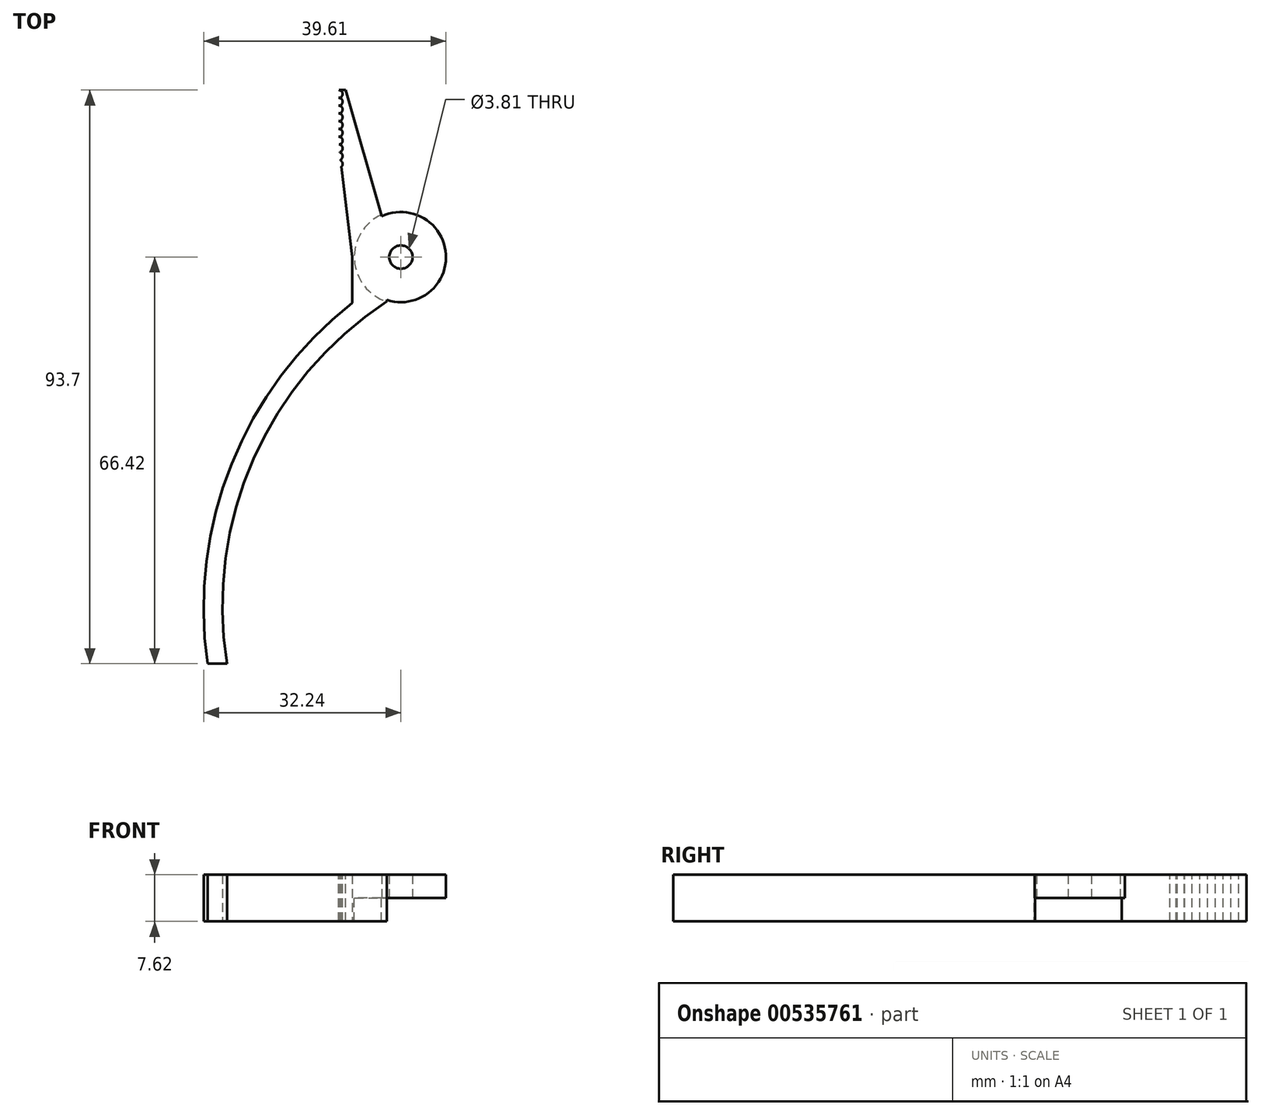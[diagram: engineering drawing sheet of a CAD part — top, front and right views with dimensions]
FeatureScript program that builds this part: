
annotation { "Feature Type Name" : "Feature", "Feature Type Description" : "" }
export const myFeature = defineFeature(function(context is Context, id is Id, definition is map)
    precondition{}
    {
        {
            var Q0;
            Q0=qCreatedBy(makeId("Top.planeOp"),FACE);
            var sketch = newSketch(context, id + "F0", { "sketchPlane" : qUnion([Q0])});
            skCircle(sketch, "E0", {"center": v(0, 0) * mm, "radius": 7.62 * mm});
            skCircle(sketch, "E1", {"center": v(0, 0) * mm, "radius": 7.37 * mm});
            skLineSegment(sketch, "E2", {"start": v(-10.16, 31.32) * mm, "end": v(-10.16, 18.62) * mm});
            skLineSegment(sketch, "E3", {"start": v(-10.16, 31.32) * mm, "end": v(-3.21, 6.91) * mm});
            skLineSegment(sketch, "E4", {"start": v(-10.16, 18.62) * mm, "end": v(-7.94, 0) * mm});
            skLineSegment(sketch, "E5", {"start": v(-7.94, 0) * mm, "end": v(-7.94, -7.49) * mm});
            skLineSegment(sketch, "E6", {"start": v(-7.94, -7.49) * mm, "end": v(-2.3, -7.26) * mm});
            skArc(sketch, "E7", {"start": v(-7.94, -7.49) * mm, "mid": v(-27.67, -33.78) * mm, "end": v(-31.6, -66.42) * mm});
            skLineSegment(sketch, "E8", {"start": v(-31.6, -66.42) * mm, "end": v(-28.43, -66.42) * mm});
            skArc(sketch, "E9", {"start": v(-2.3, -7.26) * mm, "mid": v(-24.1, -32.99) * mm, "end": v(-28.43, -66.42) * mm});
            skCircle(sketch, "E10", {"center": v(0, 0) * mm, "radius": 1.9 * mm});
            skLineSegment(sketch, "E11", {"start": v(-2.3, -7.26) * mm, "end": v(-2.3, -7) * mm});
            skLineSegment(sketch, "E12", {"start": v(-3.21, 6.91) * mm, "end": v(-3.14, 6.66) * mm});
            skSolve(sketch);
        }
        {
            var Q0;
            Q0=makeQuery(id+"F0.imprint","IMPRINT",FACE,{"disambiguationData":[TD([[makeQuery(id+"F0.imprint","IMPRINT",EDGE,{"derivedFrom":sQuery(id+"F0.wireOp",EDGE,"E6")}),-1.0]])]});
            var Q1;
            {var subQ0=sQuery(id+"F0.wireOp",EDGE,"E5");Q1=makeQuery(id+"F0.imprint","IMPRINT",FACE,{"disambiguationData":[TD([[makeQuery(id+"F0.imprint","IMPRINT",EDGE,{"derivedFrom":subQ0}),1.0]])]});}
            var Q2;
            Q2=makeQuery(id+"F0.imprint","IMPRINT",FACE,{"disambiguationData":[TD([[makeQuery(id+"F0.imprint","IMPRINT",EDGE,{"derivedFrom":sQuery(id+"F0.wireOp",EDGE,"E2")}),1.0]])]});
            var Q3;
            {var subQ0=sQuery(id+"F0.wireOp",EDGE,"E7");Q3=makeQuery(id+"F0.imprint","IMPRINT",FACE,{"disambiguationData":[TD([[makeQuery(id+"F0.imprint","IMPRINT",EDGE,{"derivedFrom":subQ0}),1.0]])]});}
            var Q4;
            Q4=makeQuery(id+"F0.imprint","IMPRINT",FACE,{"disambiguationData":[TD([[makeQuery(id+"F0.imprint","IMPRINT",EDGE,{"derivedFrom":sQuery(id+"F0.wireOp",EDGE,"E10")}),-1.0]])]});
            var Q5;
            {var subQ0=sQuery(id+"F0.wireOp",EDGE,"E11");Q5=makeQuery(id+"F0.imprint","IMPRINT",FACE,{"disambiguationData":[TD([[makeQuery(id+"F0.imprint","IMPRINT",EDGE,{"derivedFrom":subQ0}),1.0]])]});}
            extrude(context, id + "F1", {"entities" : qUnion([Q0, Q1, Q2, Q3, Q4, Q5]), "depth" : 3.8 * mm, "offsetDistance" : 25.4 * mm});
        }
        {
            var Q0;
            Q0=makeQuery(id+"F0.imprint","IMPRINT",FACE,{"disambiguationData":[TD([[makeQuery(id+"F0.imprint","IMPRINT",EDGE,{"derivedFrom":sQuery(id+"F0.wireOp",EDGE,"E2")}),1.0]])]});
            var Q1;
            {var subQ0=sQuery(id+"F0.wireOp",EDGE,"E7");Q1=makeQuery(id+"F0.imprint","IMPRINT",FACE,{"disambiguationData":[TD([[makeQuery(id+"F0.imprint","IMPRINT",EDGE,{"derivedFrom":subQ0}),1.0]])]});}
            extrude(context, id + "F2", {"entities" : qUnion([Q0, Q1]), "operationType" : NewBodyOperationType.ADD, "oppositeDirection" : true, "depth" : 3.8 * mm, "offsetDistance" : 25.4 * mm});
        }
        {
            var Q0;
            Q0=makeQuery(id+"F1.opExtrude","CAP_FACE",FACE,{"disambiguationData":[OSD([sQuery(id+"F0.wireOp",EDGE,"E1"),sQuery(id+"F0.wireOp",EDGE,"E2"),sQuery(id+"F0.wireOp",EDGE,"E3"),sQuery(id+"F0.wireOp",EDGE,"E4"),sQuery(id+"F0.wireOp",EDGE,"E5"),sQuery(id+"F0.wireOp",EDGE,"E7"),sQuery(id+"F0.wireOp",EDGE,"E8"),sQuery(id+"F0.wireOp",EDGE,"E9"),sQuery(id+"F0.wireOp",EDGE,"E10"),sQuery(id+"F0.wireOp",EDGE,"E11"),sQuery(id+"F0.wireOp",EDGE,"E12")])],"isStart":false});
            var sketch = newSketch(context, id + "F3", { "sketchPlane" : qUnion([Q0])});
            skCircle(sketch, "E13", {"center": v(-10.16, 15.22) * mm, "radius": 0.64 * mm});
            skLineSegment(sketch, "E14.direction1", {"start": v(-10.16, 15.22) * mm, "end": v(15.24, 15.22) * mm, "construction": true});
            skLineSegment(sketch, "E14.direction2", {"start": v(-10.16, 15.22) * mm, "end": v(-10.16, 16.5) * mm, "construction": true});
            skPoint(sketch, "E15.0", {"position": v(-10.16, 31.32) * mm});
            skLineSegment(sketch, "E16", {"start": v(-10.16, 27.28) * mm, "end": v(-10.16, 31.32) * mm});
            skLineSegment(sketch, "E17", {"start": v(-10.16, 27.28) * mm, "end": v(-9.01, 27.28) * mm});
            skLineSegment(sketch, "E18", {"start": v(-9.01, 27.28) * mm, "end": v(-10.16, 31.32) * mm});
            skCircle(sketch, "E19.0.0.1", {"center": v(-10.16, 16.5) * mm, "radius": 0.64 * mm});
            skCircle(sketch, "E19.0.0.2", {"center": v(-10.16, 17.76) * mm, "radius": 0.64 * mm});
            skCircle(sketch, "E19.0.0.3", {"center": v(-10.16, 19.03) * mm, "radius": 0.64 * mm});
            skCircle(sketch, "E19.0.0.4", {"center": v(-10.16, 20.3) * mm, "radius": 0.64 * mm});
            skCircle(sketch, "E19.0.0.5", {"center": v(-10.16, 21.57) * mm, "radius": 0.64 * mm});
            skCircle(sketch, "E19.0.0.6", {"center": v(-10.16, 22.84) * mm, "radius": 0.64 * mm});
            skCircle(sketch, "E19.0.0.7", {"center": v(-10.16, 24.11) * mm, "radius": 0.64 * mm});
            skCircle(sketch, "E19.0.0.8", {"center": v(-10.16, 25.38) * mm, "radius": 0.64 * mm});
            skCircle(sketch, "E19.0.0.9", {"center": v(-10.16, 26.65) * mm, "radius": 0.64 * mm});
            skCircle(sketch, "E19.0.0.10", {"center": v(-10.16, 27.92) * mm, "radius": 0.64 * mm});
            skSolve(sketch);
        }
        {
            var Q0;
            Q0=makeQuery(id+"F3.imprint","IMPRINT",FACE,{"disambiguationData":[TD([[makeQuery(id+"F3.imprint","IMPRINT",EDGE,{"derivedFrom":sQuery(id+"F3.wireOp",EDGE,"E16")}),1.0]])]});
            var Q1;
            {var subQ0=sQuery(id+"F3.wireOp",EDGE,"E14.0.21.0");var subQ1=makeQuery(id+"F1.opExtrude","CAP_EDGE",EDGE,{"disambiguationData":[OSD([sQuery(id+"F0.wireOp",EDGE,"E2")])],"isStart":false});var subQ3=makeQuery(id+"F3.imprint","INTERSECT",VERTEX,{"derivedFrom":[subQ1,sQuery(id+"F3.wireOp",EDGE,"E14.0.20.0"),subQ0]});Q1=makeQuery(id+"F3.imprint","IMPRINT",FACE,{"disambiguationData":[TD([[makeQuery(id+"F3.imprint","IMPRINT",EDGE,{"disambiguationData":[TD([[subQ3,-1.0]])],"derivedFrom":subQ0}),1.0]])]});}
            var Q2;
            {var subQ0=sQuery(id+"F3.wireOp",EDGE,"E14.0.20.0");var subQ1=makeQuery(id+"F1.opExtrude","CAP_EDGE",EDGE,{"disambiguationData":[OSD([sQuery(id+"F0.wireOp",EDGE,"E2")])],"isStart":false});var subQ2=makeQuery(id+"F3.imprint","INTERSECT",VERTEX,{"derivedFrom":[subQ1,sQuery(id+"F3.wireOp",EDGE,"E14.0.19.0"),subQ0]});Q2=makeQuery(id+"F3.imprint","IMPRINT",FACE,{"disambiguationData":[TD([[makeQuery(id+"F3.imprint","IMPRINT",EDGE,{"disambiguationData":[TD([[subQ2,-1.0]])],"derivedFrom":subQ0}),1.0]])]});}
            var Q3;
            {var subQ0=sQuery(id+"F3.wireOp",EDGE,"E14.0.19.0");var subQ1=makeQuery(id+"F1.opExtrude","CAP_EDGE",EDGE,{"disambiguationData":[OSD([sQuery(id+"F0.wireOp",EDGE,"E2")])],"isStart":false});var subQ2=makeQuery(id+"F3.imprint","INTERSECT",VERTEX,{"derivedFrom":[subQ1,sQuery(id+"F3.wireOp",EDGE,"E14.0.18.0"),subQ0]});Q3=makeQuery(id+"F3.imprint","IMPRINT",FACE,{"disambiguationData":[TD([[makeQuery(id+"F3.imprint","IMPRINT",EDGE,{"disambiguationData":[TD([[subQ2,-1.0]])],"derivedFrom":subQ0}),1.0]])]});}
            var Q4;
            {var subQ0=sQuery(id+"F3.wireOp",EDGE,"E14.0.18.0");var subQ1=makeQuery(id+"F1.opExtrude","CAP_EDGE",EDGE,{"disambiguationData":[OSD([sQuery(id+"F0.wireOp",EDGE,"E2")])],"isStart":false});var subQ2=makeQuery(id+"F3.imprint","INTERSECT",VERTEX,{"derivedFrom":[subQ1,sQuery(id+"F3.wireOp",EDGE,"E14.0.17.0"),subQ0]});Q4=makeQuery(id+"F3.imprint","IMPRINT",FACE,{"disambiguationData":[TD([[makeQuery(id+"F3.imprint","IMPRINT",EDGE,{"disambiguationData":[TD([[subQ2,-1.0]])],"derivedFrom":subQ0}),1.0]])]});}
            var Q5;
            {var subQ0=sQuery(id+"F3.wireOp",EDGE,"E14.0.17.0");var subQ1=makeQuery(id+"F1.opExtrude","CAP_EDGE",EDGE,{"disambiguationData":[OSD([sQuery(id+"F0.wireOp",EDGE,"E2")])],"isStart":false});var subQ2=makeQuery(id+"F3.imprint","INTERSECT",VERTEX,{"derivedFrom":[subQ1,sQuery(id+"F3.wireOp",EDGE,"E14.0.16.0"),subQ0]});Q5=makeQuery(id+"F3.imprint","IMPRINT",FACE,{"disambiguationData":[TD([[makeQuery(id+"F3.imprint","IMPRINT",EDGE,{"disambiguationData":[TD([[subQ2,-1.0]])],"derivedFrom":subQ0}),1.0]])]});}
            var Q6;
            {var subQ0=sQuery(id+"F3.wireOp",EDGE,"E14.0.16.0");var subQ1=makeQuery(id+"F1.opExtrude","CAP_EDGE",EDGE,{"disambiguationData":[OSD([sQuery(id+"F0.wireOp",EDGE,"E2")])],"isStart":false});var subQ2=makeQuery(id+"F3.imprint","INTERSECT",VERTEX,{"derivedFrom":[subQ1,sQuery(id+"F3.wireOp",EDGE,"E14.0.15.0"),subQ0]});Q6=makeQuery(id+"F3.imprint","IMPRINT",FACE,{"disambiguationData":[TD([[makeQuery(id+"F3.imprint","IMPRINT",EDGE,{"disambiguationData":[TD([[subQ2,-1.0]])],"derivedFrom":subQ0}),1.0]])]});}
            var Q7;
            {var subQ0=sQuery(id+"F3.wireOp",EDGE,"E14.0.15.0");var subQ1=makeQuery(id+"F1.opExtrude","CAP_EDGE",EDGE,{"disambiguationData":[OSD([sQuery(id+"F0.wireOp",EDGE,"E2")])],"isStart":false});var subQ2=makeQuery(id+"F3.imprint","INTERSECT",VERTEX,{"derivedFrom":[subQ1,sQuery(id+"F3.wireOp",EDGE,"E14.0.14.0"),subQ0]});Q7=makeQuery(id+"F3.imprint","IMPRINT",FACE,{"disambiguationData":[TD([[makeQuery(id+"F3.imprint","IMPRINT",EDGE,{"disambiguationData":[TD([[subQ2,-1.0]])],"derivedFrom":subQ0}),1.0]])]});}
            var Q8;
            {var subQ0=sQuery(id+"F3.wireOp",EDGE,"E14.0.14.0");var subQ1=makeQuery(id+"F1.opExtrude","CAP_EDGE",EDGE,{"disambiguationData":[OSD([sQuery(id+"F0.wireOp",EDGE,"E2")])],"isStart":false});var subQ2=makeQuery(id+"F3.imprint","INTERSECT",VERTEX,{"derivedFrom":[subQ1,sQuery(id+"F3.wireOp",EDGE,"E14.0.13.0"),subQ0]});Q8=makeQuery(id+"F3.imprint","IMPRINT",FACE,{"disambiguationData":[TD([[makeQuery(id+"F3.imprint","IMPRINT",EDGE,{"disambiguationData":[TD([[subQ2,-1.0]])],"derivedFrom":subQ0}),1.0]])]});}
            var Q9;
            {var subQ0=sQuery(id+"F3.wireOp",EDGE,"E14.0.13.0");var subQ1=makeQuery(id+"F1.opExtrude","CAP_EDGE",EDGE,{"disambiguationData":[OSD([sQuery(id+"F0.wireOp",EDGE,"E2")])],"isStart":false});var subQ2=makeQuery(id+"F3.imprint","INTERSECT",VERTEX,{"derivedFrom":[subQ1,sQuery(id+"F3.wireOp",EDGE,"E14.0.12.0"),subQ0]});Q9=makeQuery(id+"F3.imprint","IMPRINT",FACE,{"disambiguationData":[TD([[makeQuery(id+"F3.imprint","IMPRINT",EDGE,{"disambiguationData":[TD([[subQ2,-1.0]])],"derivedFrom":subQ0}),1.0]])]});}
            var Q10;
            {var subQ0=sQuery(id+"F3.wireOp",EDGE,"E14.0.12.0");var subQ1=makeQuery(id+"F1.opExtrude","CAP_EDGE",EDGE,{"disambiguationData":[OSD([sQuery(id+"F0.wireOp",EDGE,"E2")])],"isStart":false});var subQ2=makeQuery(id+"F3.imprint","INTERSECT",VERTEX,{"derivedFrom":[subQ1,sQuery(id+"F3.wireOp",EDGE,"E14.0.11.0"),subQ0]});Q10=makeQuery(id+"F3.imprint","IMPRINT",FACE,{"disambiguationData":[TD([[makeQuery(id+"F3.imprint","IMPRINT",EDGE,{"disambiguationData":[TD([[subQ2,-1.0]])],"derivedFrom":subQ0}),1.0]])]});}
            var Q11;
            {var subQ0=sQuery(id+"F3.wireOp",EDGE,"E14.0.11.0");var subQ1=makeQuery(id+"F1.opExtrude","CAP_EDGE",EDGE,{"disambiguationData":[OSD([sQuery(id+"F0.wireOp",EDGE,"E2")])],"isStart":false});var subQ2=makeQuery(id+"F3.imprint","INTERSECT",VERTEX,{"derivedFrom":[subQ1,sQuery(id+"F3.wireOp",EDGE,"E14.0.10.0"),subQ0]});Q11=makeQuery(id+"F3.imprint","IMPRINT",FACE,{"disambiguationData":[TD([[makeQuery(id+"F3.imprint","IMPRINT",EDGE,{"disambiguationData":[TD([[subQ2,-1.0]])],"derivedFrom":subQ0}),1.0]])]});}
            var Q12;
            {var subQ0=sQuery(id+"F3.wireOp",EDGE,"E14.0.10.0");var subQ1=makeQuery(id+"F1.opExtrude","CAP_EDGE",EDGE,{"disambiguationData":[OSD([sQuery(id+"F0.wireOp",EDGE,"E2")])],"isStart":false});var subQ2=makeQuery(id+"F3.imprint","INTERSECT",VERTEX,{"derivedFrom":[subQ1,sQuery(id+"F3.wireOp",EDGE,"E14.0.9.0"),subQ0]});Q12=makeQuery(id+"F3.imprint","IMPRINT",FACE,{"disambiguationData":[TD([[makeQuery(id+"F3.imprint","IMPRINT",EDGE,{"disambiguationData":[TD([[subQ2,-1.0]])],"derivedFrom":subQ0}),1.0]])]});}
            var Q13;
            {var subQ0=sQuery(id+"F3.wireOp",EDGE,"E14.0.9.0");var subQ1=makeQuery(id+"F1.opExtrude","CAP_EDGE",EDGE,{"disambiguationData":[OSD([sQuery(id+"F0.wireOp",EDGE,"E2")])],"isStart":false});var subQ2=makeQuery(id+"F3.imprint","INTERSECT",VERTEX,{"derivedFrom":[subQ1,sQuery(id+"F3.wireOp",EDGE,"E14.0.8.0"),subQ0]});Q13=makeQuery(id+"F3.imprint","IMPRINT",FACE,{"disambiguationData":[TD([[makeQuery(id+"F3.imprint","IMPRINT",EDGE,{"disambiguationData":[TD([[subQ2,-1.0]])],"derivedFrom":subQ0}),1.0]])]});}
            var Q14;
            {var subQ0=sQuery(id+"F3.wireOp",EDGE,"E14.0.8.0");var subQ1=makeQuery(id+"F1.opExtrude","CAP_EDGE",EDGE,{"disambiguationData":[OSD([sQuery(id+"F0.wireOp",EDGE,"E2")])],"isStart":false});var subQ2=makeQuery(id+"F3.imprint","INTERSECT",VERTEX,{"derivedFrom":[subQ1,sQuery(id+"F3.wireOp",EDGE,"E14.0.7.0"),subQ0]});Q14=makeQuery(id+"F3.imprint","IMPRINT",FACE,{"disambiguationData":[TD([[makeQuery(id+"F3.imprint","IMPRINT",EDGE,{"disambiguationData":[TD([[subQ2,-1.0]])],"derivedFrom":subQ0}),1.0]])]});}
            var Q15;
            {var subQ0=sQuery(id+"F3.wireOp",EDGE,"E14.0.7.0");var subQ1=makeQuery(id+"F1.opExtrude","CAP_EDGE",EDGE,{"disambiguationData":[OSD([sQuery(id+"F0.wireOp",EDGE,"E2")])],"isStart":false});var subQ2=makeQuery(id+"F3.imprint","INTERSECT",VERTEX,{"derivedFrom":[subQ1,sQuery(id+"F3.wireOp",EDGE,"E14.0.6.0"),subQ0]});Q15=makeQuery(id+"F3.imprint","IMPRINT",FACE,{"disambiguationData":[TD([[makeQuery(id+"F3.imprint","IMPRINT",EDGE,{"disambiguationData":[TD([[subQ2,-1.0]])],"derivedFrom":subQ0}),1.0]])]});}
            var Q16;
            {var subQ0=sQuery(id+"F3.wireOp",EDGE,"E14.0.6.0");var subQ1=makeQuery(id+"F1.opExtrude","CAP_EDGE",EDGE,{"disambiguationData":[OSD([sQuery(id+"F0.wireOp",EDGE,"E2")])],"isStart":false});var subQ2=makeQuery(id+"F3.imprint","INTERSECT",VERTEX,{"derivedFrom":[subQ1,sQuery(id+"F3.wireOp",EDGE,"E14.0.5.0"),subQ0]});Q16=makeQuery(id+"F3.imprint","IMPRINT",FACE,{"disambiguationData":[TD([[makeQuery(id+"F3.imprint","IMPRINT",EDGE,{"disambiguationData":[TD([[subQ2,-1.0]])],"derivedFrom":subQ0}),1.0]])]});}
            var Q17;
            {var subQ0=sQuery(id+"F3.wireOp",EDGE,"E14.0.5.0");var subQ1=makeQuery(id+"F1.opExtrude","CAP_EDGE",EDGE,{"disambiguationData":[OSD([sQuery(id+"F0.wireOp",EDGE,"E2")])],"isStart":false});var subQ2=makeQuery(id+"F3.imprint","INTERSECT",VERTEX,{"derivedFrom":[subQ1,sQuery(id+"F3.wireOp",EDGE,"E14.0.4.0"),subQ0]});Q17=makeQuery(id+"F3.imprint","IMPRINT",FACE,{"disambiguationData":[TD([[makeQuery(id+"F3.imprint","IMPRINT",EDGE,{"disambiguationData":[TD([[subQ2,-1.0]])],"derivedFrom":subQ0}),1.0]])]});}
            var Q18;
            {var subQ0=sQuery(id+"F3.wireOp",EDGE,"E14.0.3.0");var subQ1=makeQuery(id+"F1.opExtrude","CAP_EDGE",EDGE,{"disambiguationData":[OSD([sQuery(id+"F0.wireOp",EDGE,"E2")])],"isStart":false});var subQ2=makeQuery(id+"F3.imprint","INTERSECT",VERTEX,{"derivedFrom":[subQ1,sQuery(id+"F3.wireOp",EDGE,"E14.0.2.0"),subQ0]});Q18=makeQuery(id+"F3.imprint","IMPRINT",FACE,{"disambiguationData":[TD([[makeQuery(id+"F3.imprint","IMPRINT",EDGE,{"disambiguationData":[TD([[subQ2,-1.0]])],"derivedFrom":subQ0}),1.0]])]});}
            var Q19;
            {var subQ0=sQuery(id+"F3.wireOp",EDGE,"E14.0.4.0");var subQ1=makeQuery(id+"F1.opExtrude","CAP_EDGE",EDGE,{"disambiguationData":[OSD([sQuery(id+"F0.wireOp",EDGE,"E2")])],"isStart":false});var subQ2=makeQuery(id+"F3.imprint","INTERSECT",VERTEX,{"derivedFrom":[subQ1,sQuery(id+"F3.wireOp",EDGE,"E14.0.3.0"),subQ0]});Q19=makeQuery(id+"F3.imprint","IMPRINT",FACE,{"disambiguationData":[TD([[makeQuery(id+"F3.imprint","IMPRINT",EDGE,{"disambiguationData":[TD([[subQ2,-1.0]])],"derivedFrom":subQ0}),1.0]])]});}
            var Q20;
            {var subQ0=sQuery(id+"F3.wireOp",EDGE,"E14.0.2.0");var subQ1=makeQuery(id+"F1.opExtrude","CAP_EDGE",EDGE,{"disambiguationData":[OSD([sQuery(id+"F0.wireOp",EDGE,"E2")])],"isStart":false});var subQ2=makeQuery(id+"F3.imprint","INTERSECT",VERTEX,{"derivedFrom":[subQ1,sQuery(id+"F3.wireOp",EDGE,"E14.0.1.0"),subQ0]});Q20=makeQuery(id+"F3.imprint","IMPRINT",FACE,{"disambiguationData":[TD([[makeQuery(id+"F3.imprint","IMPRINT",EDGE,{"disambiguationData":[TD([[subQ2,-1.0]])],"derivedFrom":subQ0}),1.0]])]});}
            var Q21;
            {var subQ0=sQuery(id+"F3.wireOp",EDGE,"E14.0.1.0");var subQ1=makeQuery(id+"F1.opExtrude","CAP_EDGE",EDGE,{"disambiguationData":[OSD([sQuery(id+"F0.wireOp",EDGE,"E2")])],"isStart":false});var subQ2=makeQuery(id+"F3.imprint","INTERSECT",VERTEX,{"derivedFrom":[subQ1,sQuery(id+"F3.wireOp",EDGE,"E13"),subQ0]});Q21=makeQuery(id+"F3.imprint","IMPRINT",FACE,{"disambiguationData":[TD([[makeQuery(id+"F3.imprint","IMPRINT",EDGE,{"disambiguationData":[TD([[subQ2,-1.0]])],"derivedFrom":subQ0}),1.0]])]});}
            var Q22;
            {var subQ1=makeQuery(id+"F1.opExtrude","CAP_EDGE",EDGE,{"disambiguationData":[OSD([sQuery(id+"F0.wireOp",EDGE,"E4")])],"isStart":false});var subQ3=makeQuery(id+"F1.opExtrude","CAP_EDGE",EDGE,{"disambiguationData":[OSD([sQuery(id+"F0.wireOp",EDGE,"E2")])],"isStart":false});var subQ5=makeQuery(id+"F3.imprint","INTERSECT",VERTEX,{"derivedFrom":[subQ3,subQ1]});Q22=makeQuery(id+"F3.imprint","IMPRINT",FACE,{"disambiguationData":[TD([[makeQuery(id+"F3.imprint","IMPRINT",EDGE,{"disambiguationData":[TD([[subQ5,-1.0]])],"derivedFrom":subQ1}),1.0]])]});}
            var Q23;
            {var subQ0=sQuery(id+"F3.wireOp",EDGE,"E17");var subQ3=sQuery(id+"F3.wireOp",EDGE,"E19.0.0.9");var subQ4=makeQuery(id+"F3.imprint","INTERSECT",VERTEX,{"derivedFrom":[subQ0,subQ3]});Q23=makeQuery(id+"F3.imprint","IMPRINT",FACE,{"disambiguationData":[TD([[makeQuery(id+"F3.imprint","IMPRINT",EDGE,{"disambiguationData":[TD([[subQ4,1.0]])],"derivedFrom":subQ0}),-1.0]])]});}
            var Q24;
            {var subQ6=sQuery(id+"F3.wireOp",EDGE,"E18");Q24=makeQuery(id+"F3.imprint","IMPRINT",FACE,{"disambiguationData":[TD([[makeQuery(id+"F3.imprint","IMPRINT",EDGE,{"derivedFrom":subQ6}),-1.0]])]});}
            var Q25;
            {var subQ0=sQuery(id+"F3.wireOp",EDGE,"E19.0.0.8");var subQ1=makeQuery(id+"F1.opExtrude","CAP_EDGE",EDGE,{"disambiguationData":[OSD([sQuery(id+"F0.wireOp",EDGE,"E2")])],"isStart":false});var subQ2=makeQuery(id+"F3.imprint","INTERSECT",VERTEX,{"derivedFrom":[subQ1,sQuery(id+"F3.wireOp",EDGE,"E19.0.0.7"),subQ0]});Q25=makeQuery(id+"F3.imprint","IMPRINT",FACE,{"disambiguationData":[TD([[makeQuery(id+"F3.imprint","IMPRINT",EDGE,{"disambiguationData":[TD([[subQ2,-1.0]])],"derivedFrom":subQ0}),1.0]])]});}
            var Q26;
            {var subQ0=sQuery(id+"F3.wireOp",EDGE,"E19.0.0.7");var subQ1=makeQuery(id+"F1.opExtrude","CAP_EDGE",EDGE,{"disambiguationData":[OSD([sQuery(id+"F0.wireOp",EDGE,"E2")])],"isStart":false});var subQ2=makeQuery(id+"F3.imprint","INTERSECT",VERTEX,{"derivedFrom":[subQ1,sQuery(id+"F3.wireOp",EDGE,"E19.0.0.6"),subQ0]});Q26=makeQuery(id+"F3.imprint","IMPRINT",FACE,{"disambiguationData":[TD([[makeQuery(id+"F3.imprint","IMPRINT",EDGE,{"disambiguationData":[TD([[subQ2,-1.0]])],"derivedFrom":subQ0}),1.0]])]});}
            var Q27;
            {var subQ0=sQuery(id+"F3.wireOp",EDGE,"E19.0.0.6");var subQ1=makeQuery(id+"F1.opExtrude","CAP_EDGE",EDGE,{"disambiguationData":[OSD([sQuery(id+"F0.wireOp",EDGE,"E2")])],"isStart":false});var subQ2=makeQuery(id+"F3.imprint","INTERSECT",VERTEX,{"derivedFrom":[subQ1,sQuery(id+"F3.wireOp",EDGE,"E19.0.0.5"),subQ0]});Q27=makeQuery(id+"F3.imprint","IMPRINT",FACE,{"disambiguationData":[TD([[makeQuery(id+"F3.imprint","IMPRINT",EDGE,{"disambiguationData":[TD([[subQ2,-1.0]])],"derivedFrom":subQ0}),1.0]])]});}
            var Q28;
            {var subQ0=sQuery(id+"F3.wireOp",EDGE,"E19.0.0.5");var subQ1=makeQuery(id+"F1.opExtrude","CAP_EDGE",EDGE,{"disambiguationData":[OSD([sQuery(id+"F0.wireOp",EDGE,"E2")])],"isStart":false});var subQ2=makeQuery(id+"F3.imprint","INTERSECT",VERTEX,{"derivedFrom":[subQ1,sQuery(id+"F3.wireOp",EDGE,"E19.0.0.4"),subQ0]});Q28=makeQuery(id+"F3.imprint","IMPRINT",FACE,{"disambiguationData":[TD([[makeQuery(id+"F3.imprint","IMPRINT",EDGE,{"disambiguationData":[TD([[subQ2,-1.0]])],"derivedFrom":subQ0}),1.0]])]});}
            var Q29;
            {var subQ0=sQuery(id+"F3.wireOp",EDGE,"E19.0.0.4");var subQ1=makeQuery(id+"F1.opExtrude","CAP_EDGE",EDGE,{"disambiguationData":[OSD([sQuery(id+"F0.wireOp",EDGE,"E2")])],"isStart":false});var subQ2=makeQuery(id+"F3.imprint","INTERSECT",VERTEX,{"derivedFrom":[subQ1,sQuery(id+"F3.wireOp",EDGE,"E19.0.0.3"),subQ0]});Q29=makeQuery(id+"F3.imprint","IMPRINT",FACE,{"disambiguationData":[TD([[makeQuery(id+"F3.imprint","IMPRINT",EDGE,{"disambiguationData":[TD([[subQ2,-1.0]])],"derivedFrom":subQ0}),1.0]])]});}
            var Q30;
            {var subQ0=sQuery(id+"F3.wireOp",EDGE,"E19.0.0.2");var subQ1=makeQuery(id+"F1.opExtrude","CAP_EDGE",EDGE,{"disambiguationData":[OSD([sQuery(id+"F0.wireOp",EDGE,"E4")])],"isStart":false});var subQ2=makeQuery(id+"F3.imprint","INTERSECT",VERTEX,{"disambiguationData":[OD(0.0)],"derivedFrom":[subQ1,subQ0]});Q30=makeQuery(id+"F3.imprint","IMPRINT",FACE,{"disambiguationData":[TD([[makeQuery(id+"F3.imprint","IMPRINT",EDGE,{"disambiguationData":[TD([[subQ2,1.0]])],"derivedFrom":subQ0}),1.0]])]});}
            var Q31;
            {var subQ0=sQuery(id+"F3.wireOp",EDGE,"E19.0.0.1");var subQ1=makeQuery(id+"F1.opExtrude","CAP_EDGE",EDGE,{"disambiguationData":[OSD([sQuery(id+"F0.wireOp",EDGE,"E4")])],"isStart":false});var subQ2=makeQuery(id+"F3.imprint","INTERSECT",VERTEX,{"disambiguationData":[OD(0.0)],"derivedFrom":[subQ1,subQ0]});Q31=makeQuery(id+"F3.imprint","IMPRINT",FACE,{"disambiguationData":[TD([[makeQuery(id+"F3.imprint","IMPRINT",EDGE,{"disambiguationData":[TD([[subQ2,1.0]])],"derivedFrom":subQ0}),1.0]])]});}
            var Q32;
            {var subQ0=sQuery(id+"F3.wireOp",EDGE,"E13");var subQ1=makeQuery(id+"F1.opExtrude","CAP_EDGE",EDGE,{"disambiguationData":[OSD([sQuery(id+"F0.wireOp",EDGE,"E4")])],"isStart":false});var subQ2=makeQuery(id+"F3.imprint","INTERSECT",VERTEX,{"disambiguationData":[OD(0.0)],"derivedFrom":[subQ1,subQ0]});Q32=makeQuery(id+"F3.imprint","IMPRINT",FACE,{"disambiguationData":[TD([[makeQuery(id+"F3.imprint","IMPRINT",EDGE,{"disambiguationData":[TD([[subQ2,-1.0]])],"derivedFrom":subQ0}),1.0]])]});}
            extrude(context, id + "F4", {"entities" : qUnion([Q0, Q1, Q2, Q3, Q4, Q5, Q6, Q7, Q8, Q9, Q10, Q11, Q12, Q13, Q14, Q15, Q16, Q17, Q18, Q19, Q20, Q21, Q22, Q23, Q24, Q25, Q26, Q27, Q28, Q29, Q30, Q31, Q32]), "operationType" : NewBodyOperationType.REMOVE, "endBound" : BoundingType.THROUGH_ALL, "oppositeDirection" : true, "depth" : 25.4 * mm, "offsetDistance" : 25.4 * mm});
        }
    });
